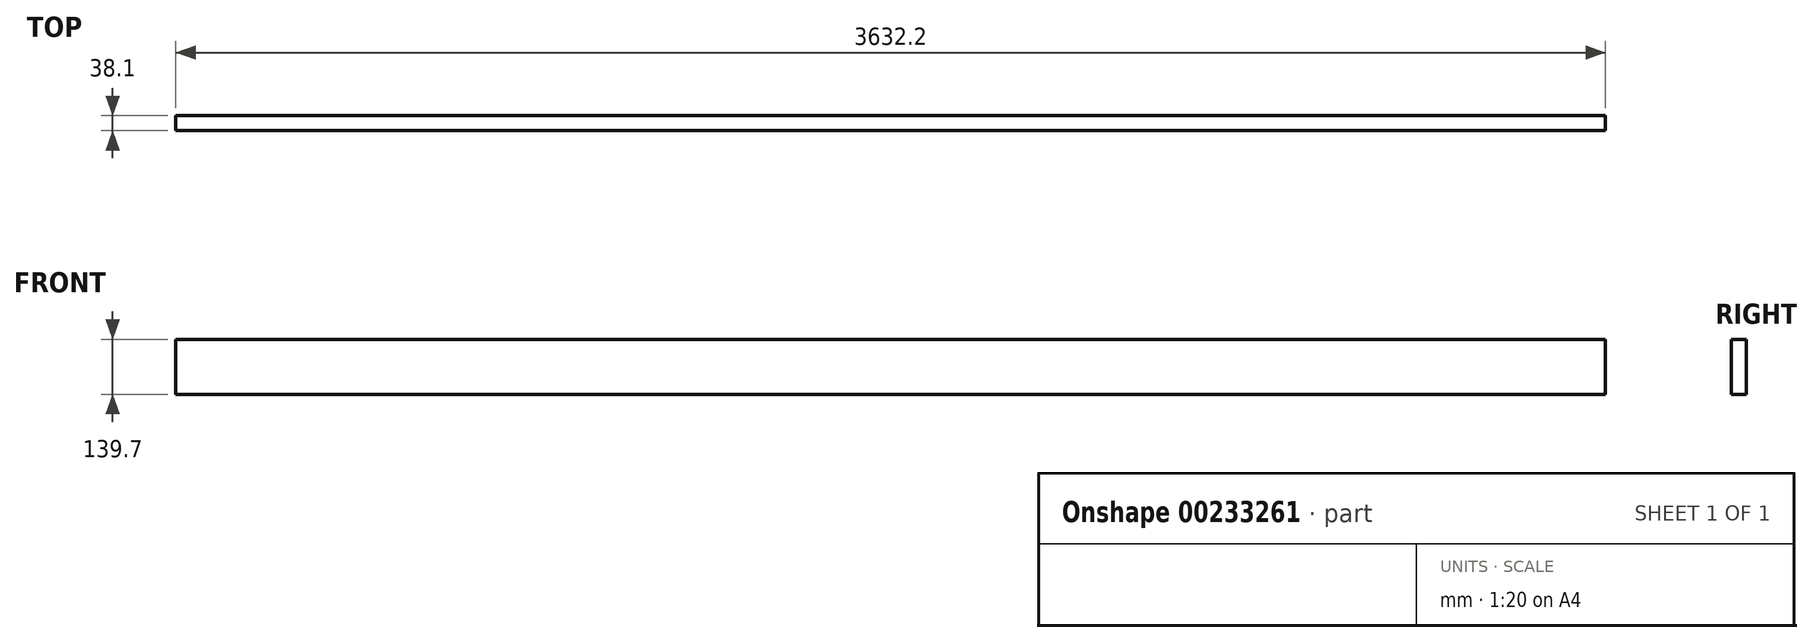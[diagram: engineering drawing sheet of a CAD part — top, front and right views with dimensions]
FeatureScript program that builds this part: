
annotation { "Feature Type Name" : "Feature", "Feature Type Description" : "" }
export const myFeature = defineFeature(function(context is Context, id is Id, definition is map)
    precondition{}
    {
        {
            var Q0;
            Q0=qCreatedBy(makeId("Front.planeOp"),FACE);
            var sketch = newSketch(context, id + "F0", { "sketchPlane" : qUnion([Q0])});
            skLineSegment(sketch, "E0", {"start": v(-2668.32, 0) * mm, "end": v(963.88, 0) * mm});
            skLineSegment(sketch, "E1", {"start": v(963.88, 0) * mm, "end": v(963.88, -139.7) * mm});
            skLineSegment(sketch, "E2", {"start": v(963.88, -139.7) * mm, "end": v(-2668.32, -139.7) * mm});
            skLineSegment(sketch, "E3", {"start": v(-2668.32, -139.7) * mm, "end": v(-2668.32, 0) * mm});
            skSolve(sketch);
        }
        {
            var Q0;
            Q0 = qSketchRegion(id + "F0", true);
            extrude(context, id + "F1", {"entities" : qUnion([Q0]), "depth" : 38.1 * mm});
        }
    });
